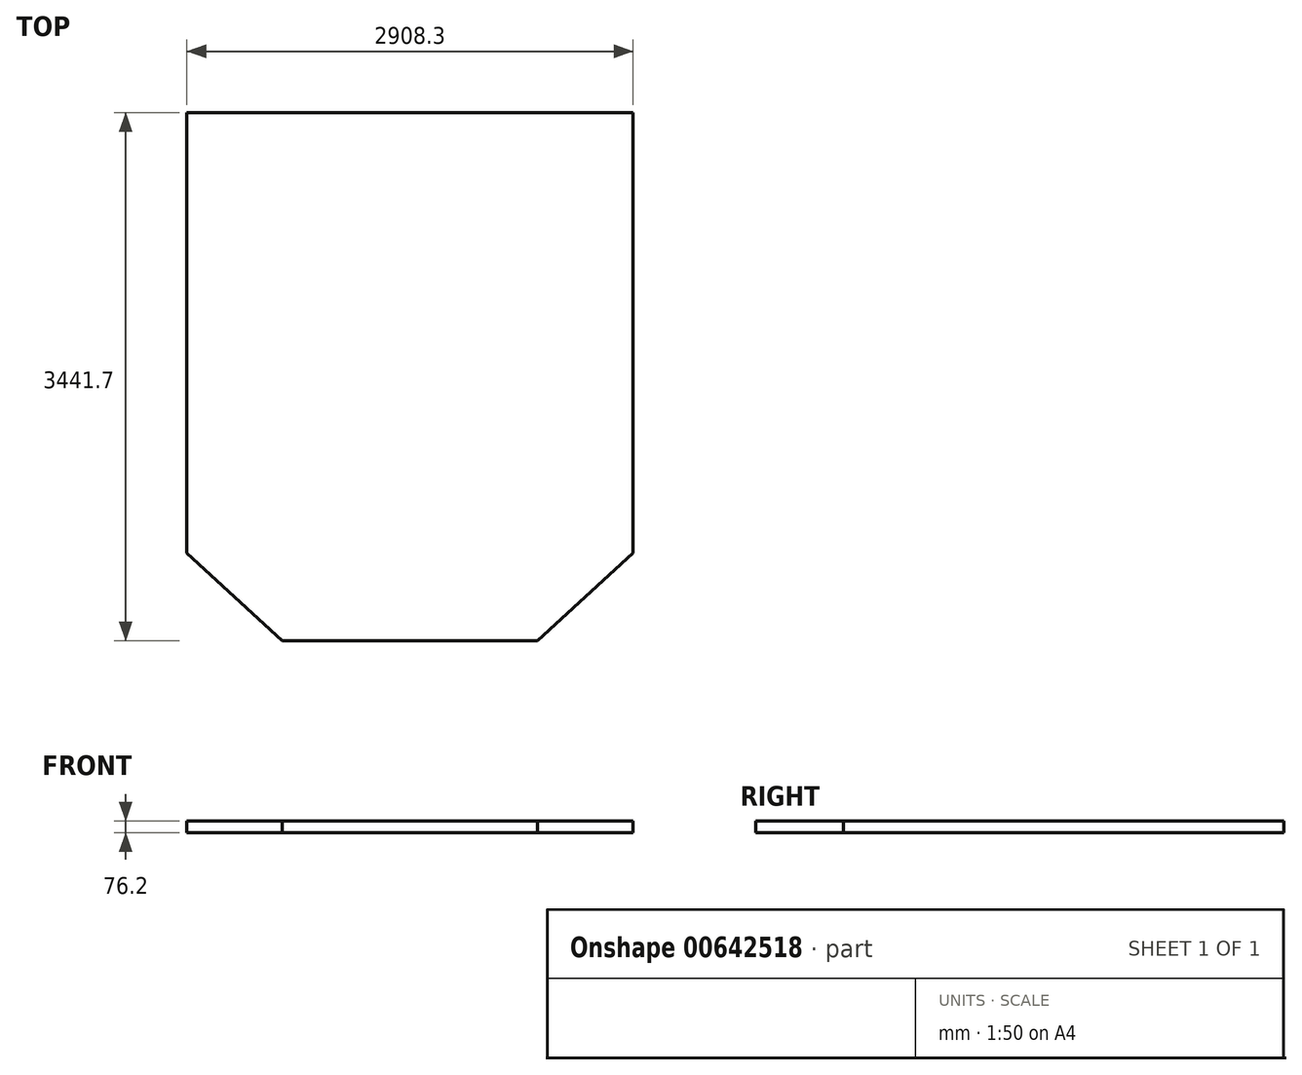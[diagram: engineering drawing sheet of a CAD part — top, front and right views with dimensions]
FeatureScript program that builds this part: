
annotation { "Feature Type Name" : "Feature", "Feature Type Description" : "" }
export const myFeature = defineFeature(function(context is Context, id is Id, definition is map)
    precondition{}
    {
        {
            var Q0;
            Q0=qCreatedBy(makeId("Top.planeOp"),FACE);
            var sketch = newSketch(context, id + "F0", { "sketchPlane" : qUnion([Q0])});
            skLineSegment(sketch, "E0", {"start": v(0, 0) * mm, "end": v(2908.3, 0) * mm});
            skLineSegment(sketch, "E1", {"start": v(2908.3, 0) * mm, "end": v(2908.3, -2870.2) * mm});
            skLineSegment(sketch, "E2", {"start": v(2908.3, -2870.2) * mm, "end": v(2286, -3441.7) * mm});
            skLineSegment(sketch, "E3", {"start": v(2286, -3441.7) * mm, "end": v(622.3, -3441.7) * mm});
            skLineSegment(sketch, "E4", {"start": v(622.3, -3441.7) * mm, "end": v(0, -2870.2) * mm});
            skLineSegment(sketch, "E5", {"start": v(0, -2870.2) * mm, "end": v(0, 0) * mm});
            skSolve(sketch);
        }
        {
            var Q0;
            Q0=makeQuery(id+"F0.imprint","IMPRINT",FACE,{"disambiguationData":[TD([[makeQuery(id+"F0.imprint","IMPRINT",EDGE,{"derivedFrom":sQuery(id+"F0.wireOp",EDGE,"E0")}),-1.0]])]});
            extrude(context, id + "F1", {"entities" : qUnion([Q0]), "depth" : 76.2 * mm, "offsetDistance" : 25.4 * mm});
        }
    });
